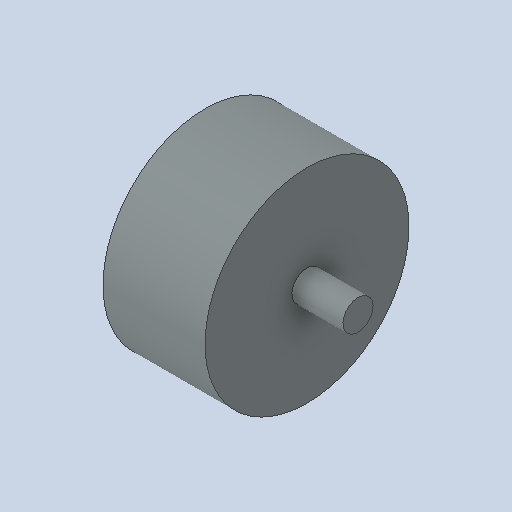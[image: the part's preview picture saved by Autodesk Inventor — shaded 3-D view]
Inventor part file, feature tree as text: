
AUTODESK INVENTOR PART (.ipt)
format: ipt  version: 2023 (Build 270158000, 158)  size: 117,248 bytes
history: native  units: mm
features: other x7, revolve x1, sketch x1
ambient origin geometry x8: Origin, YZ Plane, XZ Plane, XY Plane, X Axis, Y Axis, Z Axis, Center Point
bodies: Solid1 (feature_tree)
feature tree (9):
  revolve  "Revolution1"  [1 undecoded]
  other  "p1_XY"
  other  "p1_YZ"
  other  "p1_ZX"
  other  "p1_X"
  other  "p1_Y"
  other  "p1_Z"
  other  "p1_Center"
  sketch  "Sketch_1"  dims[d0=360.0deg]
note: 1 required parameter value undecoded (feature->parameter linkage not recoverable at this tier; creation-order binding heuristic only, values carry confidence <= 0.55)
